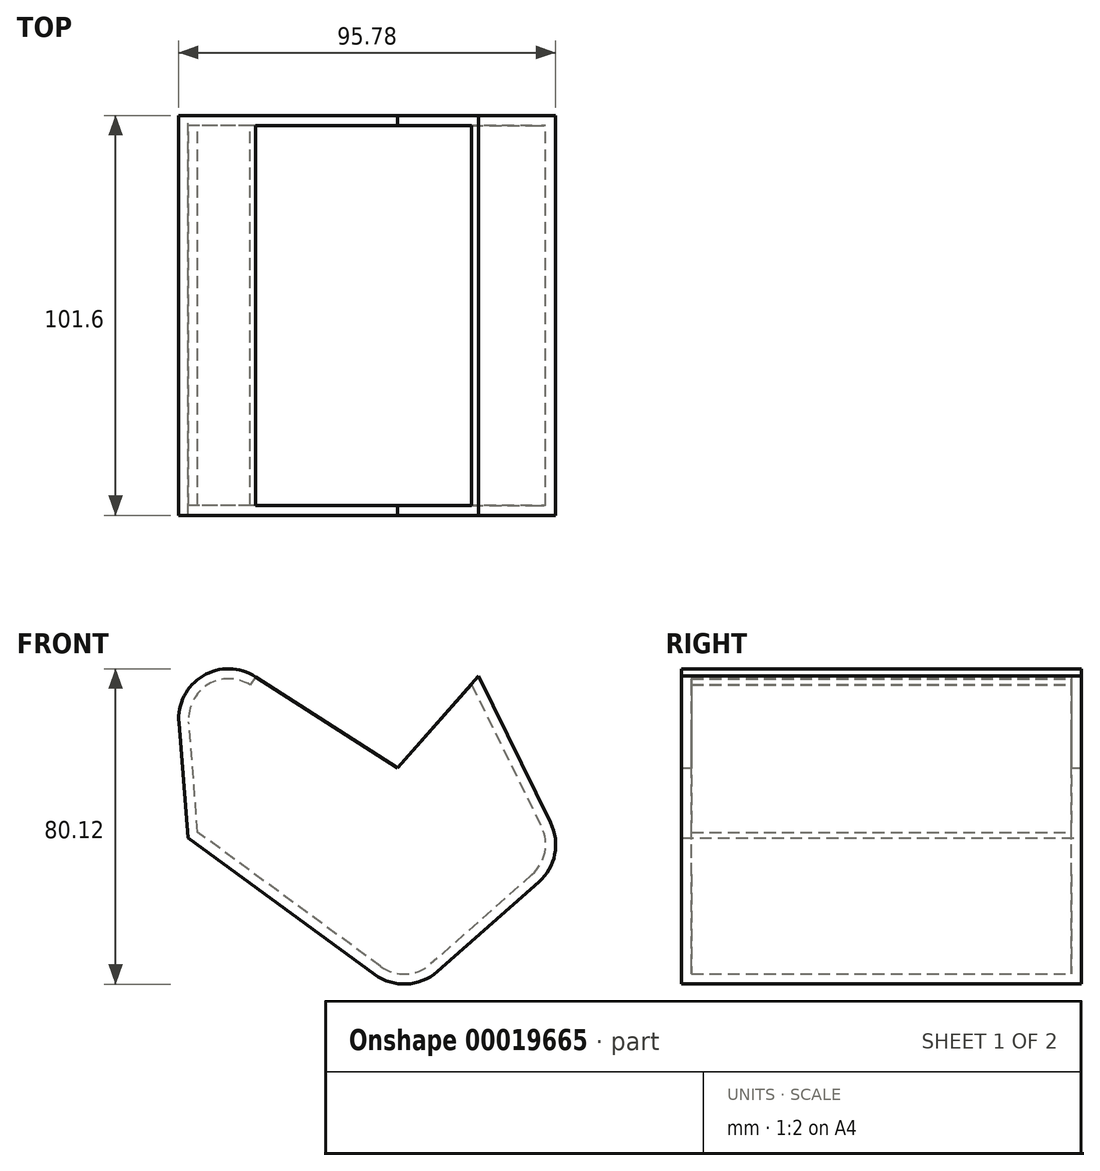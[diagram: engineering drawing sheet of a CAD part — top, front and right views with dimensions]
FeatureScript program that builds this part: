
annotation { "Feature Type Name" : "Feature", "Feature Type Description" : "" }
export const myFeature = defineFeature(function(context is Context, id is Id, definition is map)
    precondition{}
    {
        {
            var Q0;
            Q0=qCreatedBy(makeId("Front.planeOp"),FACE);
            var sketch = newSketch(context, id + "F0", { "sketchPlane" : qUnion([Q0])});
            skLineSegment(sketch, "E0", {"start": v(-147.55, 76.33) * mm, "end": v(-89.9, 39.36) * mm});
            skLineSegment(sketch, "E1", {"start": v(-89.9, 39.36) * mm, "end": v(-69.34, 62.63) * mm});
            skLineSegment(sketch, "E2", {"start": v(-69.34, 62.63) * mm, "end": v(-46.76, 16.74) * mm});
            skLineSegment(sketch, "E3", {"start": v(-46.76, 16.74) * mm, "end": v(-87.48, -19.2) * mm});
            skLineSegment(sketch, "E4", {"start": v(-87.48, -19.2) * mm, "end": v(-143.11, 21.58) * mm});
            skLineSegment(sketch, "E5", {"start": v(-143.11, 21.58) * mm, "end": v(-147.55, 76.33) * mm});
            skSolve(sketch);
        }
        {
            var Q0;
            Q0=makeQuery(id+"F0.imprint","IMPRINT",FACE,{"disambiguationData":[TD([[makeQuery(id+"F0.imprint","IMPRINT",EDGE,{"derivedFrom":sQuery(id+"F0.wireOp",EDGE,"E0")}),-1.0]])]});
            extrude(context, id + "F1", {"entities" : qUnion([Q0]), "depth" : 101.6 * mm});
        }
        {
            var Q0;
            Q0=makeQuery(id+"F1.opExtrude","SWEPT_EDGE",EDGE,{"disambiguationData":[OSD([sQuery(id+"F0.wireOp",EDGE,"E2"),sQuery(id+"F0.wireOp",EDGE,"E3")])]});
            var Q1;
            Q1=makeQuery(id+"F1.opExtrude","SWEPT_EDGE",EDGE,{"disambiguationData":[OSD([sQuery(id+"F0.wireOp",EDGE,"E3"),sQuery(id+"F0.wireOp",EDGE,"E4")])]});
            var Q2;
            Q2=makeQuery(id+"F1.opExtrude","SWEPT_EDGE",EDGE,{"disambiguationData":[OSD([sQuery(id+"F0.wireOp",EDGE,"E0"),sQuery(id+"F0.wireOp",EDGE,"E5")])]});
            fillet(context, id + "F2", {"entities" : qUnion([Q0, Q1, Q2]), "radius" : 12.7 * mm, "tangentPropagation" : true, "allowEdgeOverflow" : false});
        }
        {
            var Q0;
            Q0=makeQuery(id+"F1.opExtrude","SWEPT_BODY",BODY,{"disambiguationData":[OSD([sQuery(id+"F0.wireOp",EDGE,"E0"),sQuery(id+"F0.wireOp",EDGE,"E1"),sQuery(id+"F0.wireOp",EDGE,"E2"),sQuery(id+"F0.wireOp",EDGE,"E3"),sQuery(id+"F0.wireOp",EDGE,"E4"),sQuery(id+"F0.wireOp",EDGE,"E5")])]});
            var Q1;
            Q1=qCreatedBy(makeId("Front.planeOp"),FACE);
            transform(context, id + "F3", {"entities" : qUnion([Q0]), "transformType" : TransformType.TRANSLATION_DISTANCE, "transformDirection" : qUnion([Q1]), "distance" : 25.4 * mm, "makeCopy" : false});
        }
        {
            var Q0;
            Q0=makeQuery(id+"F1.opExtrude","SWEPT_FACE",FACE,{"disambiguationData":[OSD([sQuery(id+"F0.wireOp",EDGE,"E0")])]});
            var Q1;
            Q1=makeQuery(id+"F1.opExtrude","SWEPT_FACE",FACE,{"disambiguationData":[OSD([sQuery(id+"F0.wireOp",EDGE,"E1")])]});
            shell(context, id + "F4", {"entities" : qUnion([Q0, Q1]), "thickness" : 2.54 * mm});
        }
    });
